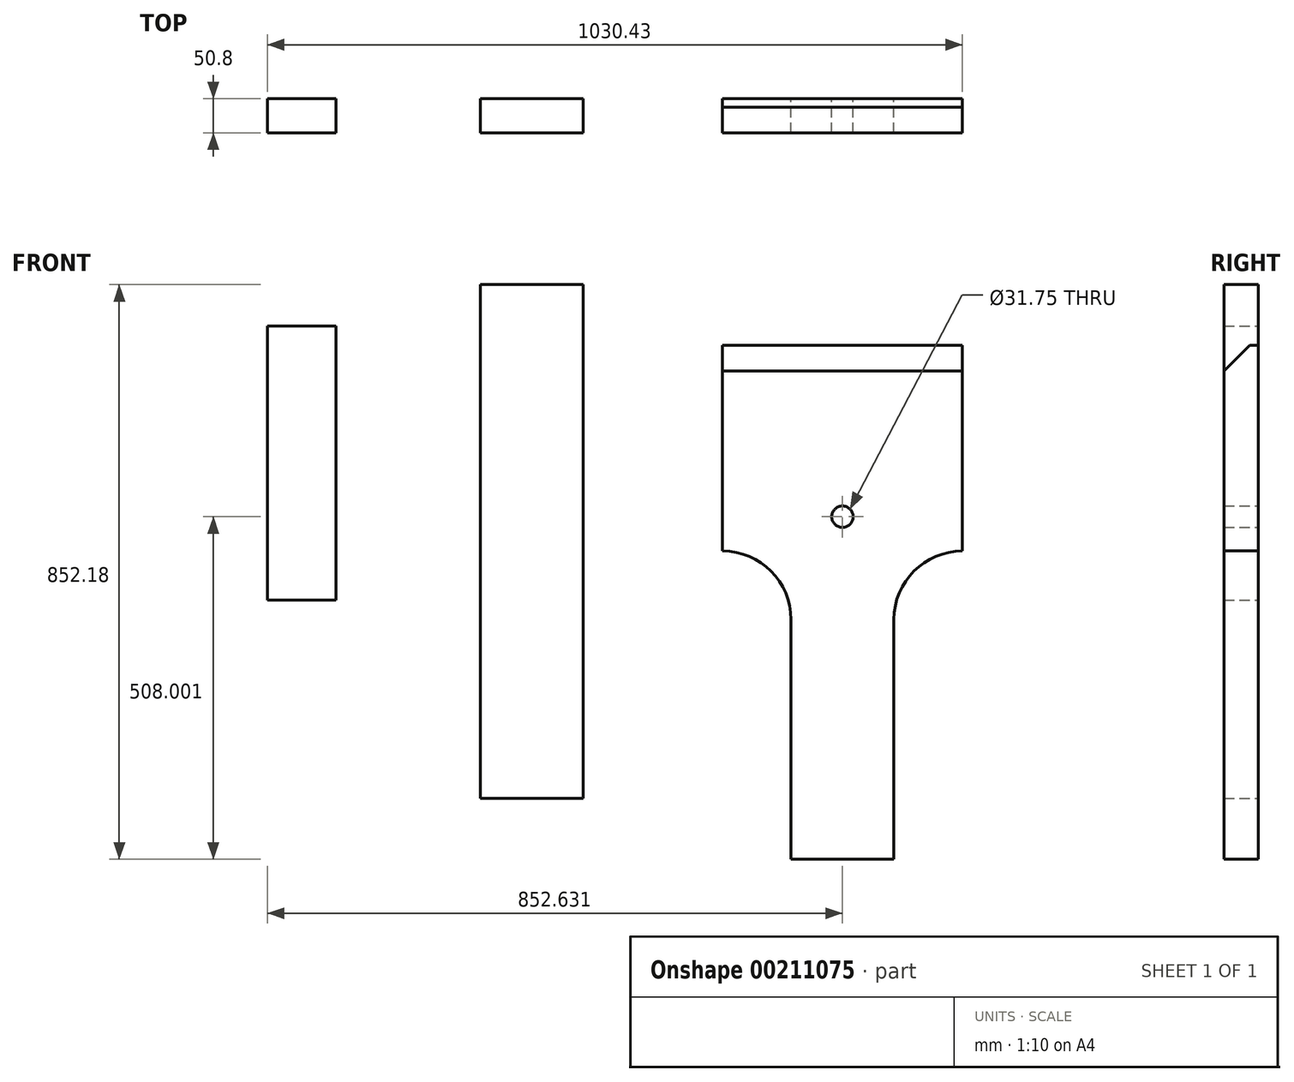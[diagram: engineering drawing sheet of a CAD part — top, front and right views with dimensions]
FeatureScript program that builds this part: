
annotation { "Feature Type Name" : "Feature", "Feature Type Description" : "" }
export const myFeature = defineFeature(function(context is Context, id is Id, definition is map)
    precondition{}
    {
        {
            var Q0;
            Q0=qCreatedBy(makeId("Front.planeOp"),FACE);
            var sketch = newSketch(context, id + "F0", { "sketchPlane" : qUnion([Q0])});
            skPoint(sketch, "E0.middle", {"position": v(0, 0) * mm});
            skLineSegment(sketch, "E1", {"start": v(-39.43, 564.64) * mm, "end": v(-39.43, -197.36) * mm, "construction": true});
            skLineSegment(sketch, "E2", {"start": v(36.77, -197.36) * mm, "end": v(36.77, 4.27) * mm});
            skLineSegment(sketch, "E3", {"start": v(138.37, 259.84) * mm, "end": v(138.37, 564.64) * mm});
            skLineSegment(sketch, "E4", {"start": v(-39.43, -197.36) * mm, "end": v(36.77, -197.36) * mm});
            skLineSegment(sketch, "E5", {"start": v(-39.43, 564.64) * mm, "end": v(138.37, 564.64) * mm});
            skLineSegment(sketch, "E6", {"start": v(138.37, 259.84) * mm, "end": v(138.37, 259.84) * mm});
            skLineSegment(sketch, "E7", {"start": v(36.77, 158.24) * mm, "end": v(36.77, 4.27) * mm});
            skPoint(sketch, "E8.visualSharp", {"position": v(36.77, 259.84) * mm});
            skArc(sketch, "E8.filletArc", {"start": v(138.37, 259.84) * mm, "mid": v(66.53, 230.08) * mm, "end": v(36.77, 158.24) * mm});
            skLineSegment(sketch, "E9.MirrorCS", {"start": v(-217.23, 259.84) * mm, "end": v(-217.23, 259.84) * mm});
            skLineSegment(sketch, "E10.MirrorCS", {"start": v(-39.43, -197.36) * mm, "end": v(-115.63, -197.36) * mm});
            skLineSegment(sketch, "E11.MirrorCS", {"start": v(-115.63, 158.24) * mm, "end": v(-115.63, 4.27) * mm});
            skPoint(sketch, "E12.MirrorP", {"position": v(-78.86, 0) * mm});
            skLineSegment(sketch, "E13.MirrorCS", {"start": v(-39.43, 564.64) * mm, "end": v(-217.23, 564.64) * mm});
            skArc(sketch, "E14.MirrorCS", {"start": v(-217.23, 259.84) * mm, "mid": v(-145.39, 230.08) * mm, "end": v(-115.63, 158.24) * mm});
            skLineSegment(sketch, "E15.MirrorCS", {"start": v(-115.63, -197.36) * mm, "end": v(-115.63, 4.27) * mm});
            skPoint(sketch, "E16.MirrorP", {"position": v(-115.63, 259.84) * mm});
            skLineSegment(sketch, "E17.MirrorCS", {"start": v(-217.23, 259.84) * mm, "end": v(-217.23, 564.64) * mm});
            skCircle(sketch, "E18", {"center": v(-39.43, 310.64) * mm, "radius": 15.88 * mm});
            skLineSegment(sketch, "E19", {"start": v(-115.63, 158.24) * mm, "end": v(-115.63, 564.64) * mm, "construction": true});
            skLineSegment(sketch, "E20", {"start": v(36.77, 158.24) * mm, "end": v(36.77, 564.64) * mm, "construction": true});
            skLineSegment(sketch, "E21.bottom", {"start": v(-576.51, -107.18) * mm, "end": v(-424.11, -107.18) * mm});
            skLineSegment(sketch, "E21.top", {"start": v(-576.51, 654.82) * mm, "end": v(-424.11, 654.82) * mm});
            skLineSegment(sketch, "E21.left", {"start": v(-576.51, -107.18) * mm, "end": v(-576.51, 654.82) * mm});
            skLineSegment(sketch, "E21.right", {"start": v(-424.11, -107.18) * mm, "end": v(-424.11, 654.82) * mm});
            skLineSegment(sketch, "E22.bottom", {"start": v(-892.06, 187.14) * mm, "end": v(-790.46, 187.14) * mm});
            skLineSegment(sketch, "E22.top", {"start": v(-892.06, 593.54) * mm, "end": v(-790.46, 593.54) * mm});
            skLineSegment(sketch, "E22.left", {"start": v(-892.06, 187.14) * mm, "end": v(-892.06, 593.54) * mm});
            skLineSegment(sketch, "E22.right", {"start": v(-790.46, 187.14) * mm, "end": v(-790.46, 593.54) * mm});
            skSolve(sketch);
        }
        {
            var Q0;
            Q0 = qSketchRegion(id + "F0", true);
            extrude(context, id + "F1", {"entities" : qUnion([Q0]), "depth" : 50.8 * mm});
        }
        {
            var Q0;
            Q0=makeQuery(id+"F1.opExtrude","CAP_EDGE",EDGE,{"disambiguationData":[OSD([sQuery(id+"F0.wireOp",EDGE,"E5"),sQuery(id+"F0.wireOp",EDGE,"E13.MirrorCS")])],"isStart":false});
            chamfer(context, id + "F2", {"entities" : qUnion([Q0]), "width" : 38.1 * mm, "tangentPropagation" : true});
        }
    });
